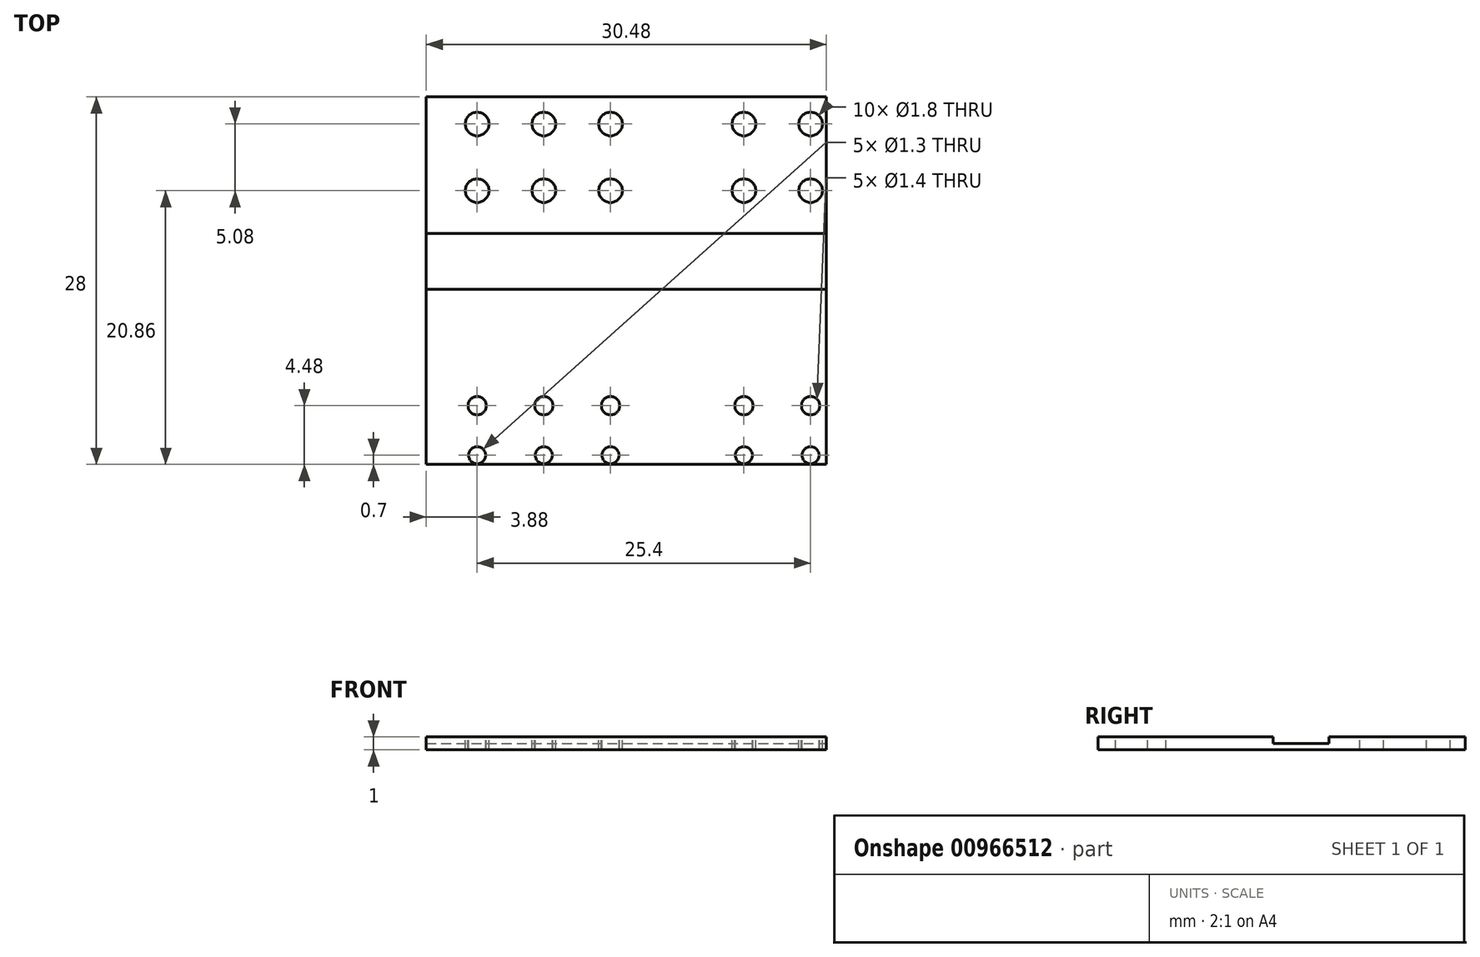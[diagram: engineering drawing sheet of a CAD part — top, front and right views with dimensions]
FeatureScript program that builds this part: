
annotation { "Feature Type Name" : "Feature", "Feature Type Description" : "" }
export const myFeature = defineFeature(function(context is Context, id is Id, definition is map)
    precondition{}
    {
        {
            var Q0;
            Q0=qCreatedBy(makeId("Top.planeOp"),FACE);
            var sketch = newSketch(context, id + "F0", { "sketchPlane" : qUnion([Q0])});
            skLineSegment(sketch, "E0.bottom", {"start": v(-15.24, 14) * mm, "end": v(15.24, 14) * mm});
            skLineSegment(sketch, "E0.top", {"start": v(-15.24, -14) * mm, "end": v(15.24, -14) * mm});
            skLineSegment(sketch, "E0.left", {"start": v(-15.24, 14) * mm, "end": v(-15.24, -14) * mm});
            skLineSegment(sketch, "E0.right", {"start": v(15.24, 14) * mm, "end": v(15.24, -14) * mm});
            skSolve(sketch);
        }
        {
            var Q0;
            Q0 = qSketchRegion(id + "F0", true);
            extrude(context, id + "F1", {"entities" : qUnion([Q0]), "depth" : 1 * mm, "offsetDistance" : 25 * mm});
        }
        {
            var Q0;
            Q0=makeQuery(id+"F1.opExtrude","CAP_FACE",FACE,{"disambiguationData":[OSD([sQuery(id+"F0.wireOp",EDGE,"E0.bottom"),sQuery(id+"F0.wireOp",EDGE,"E0.top"),sQuery(id+"F0.wireOp",EDGE,"E0.left"),sQuery(id+"F0.wireOp",EDGE,"E0.right")])],"isStart":false});
            var sketch = newSketch(context, id + "F2", { "sketchPlane" : qUnion([Q0])});
            skCircle(sketch, "E1", {"center": v(-11.36, 11.94) * mm, "radius": 0.9 * mm});
            skCircle(sketch, "E2", {"center": v(-11.36, 6.86) * mm, "radius": 0.9 * mm});
            skCircle(sketch, "E3", {"center": v(-6.28, 11.94) * mm, "radius": 0.9 * mm});
            skCircle(sketch, "E4", {"center": v(-6.28, 6.86) * mm, "radius": 0.9 * mm});
            skCircle(sketch, "E5", {"center": v(-11.36, -9.52) * mm, "radius": 0.7 * mm});
            skCircle(sketch, "E6", {"center": v(-11.36, -13.3) * mm, "radius": 0.65 * mm});
            skCircle(sketch, "E7", {"center": v(-6.28, -9.52) * mm, "radius": 0.7 * mm});
            skCircle(sketch, "E8", {"center": v(-6.28, -13.3) * mm, "radius": 0.65 * mm});
            skCircle(sketch, "E9", {"center": v(-1.2, 11.94) * mm, "radius": 0.9 * mm});
            skCircle(sketch, "E10", {"center": v(-1.2, 6.86) * mm, "radius": 0.9 * mm});
            skCircle(sketch, "E11", {"center": v(8.96, 11.94) * mm, "radius": 0.9 * mm});
            skCircle(sketch, "E12", {"center": v(8.96, 6.86) * mm, "radius": 0.9 * mm});
            skCircle(sketch, "E13", {"center": v(14.04, 11.94) * mm, "radius": 0.9 * mm});
            skCircle(sketch, "E14", {"center": v(14.04, 6.86) * mm, "radius": 0.9 * mm});
            skCircle(sketch, "E15", {"center": v(-1.2, -9.52) * mm, "radius": 0.7 * mm});
            skCircle(sketch, "E16", {"center": v(-1.2, -13.3) * mm, "radius": 0.65 * mm});
            skCircle(sketch, "E17", {"center": v(8.96, -9.52) * mm, "radius": 0.7 * mm});
            skCircle(sketch, "E18", {"center": v(8.96, -13.3) * mm, "radius": 0.65 * mm});
            skCircle(sketch, "E19", {"center": v(14.04, -9.52) * mm, "radius": 0.7 * mm});
            skCircle(sketch, "E20", {"center": v(14.04, -13.3) * mm, "radius": 0.65 * mm});
            skSolve(sketch);
        }
        {
            var Q0;
            Q0=makeQuery(id+"F1.opExtrude","CAP_FACE",FACE,{"disambiguationData":[OSD([sQuery(id+"F0.wireOp",EDGE,"E0.bottom"),sQuery(id+"F0.wireOp",EDGE,"E0.top"),sQuery(id+"F0.wireOp",EDGE,"E0.left"),sQuery(id+"F0.wireOp",EDGE,"E0.right")])],"isStart":false});
            var sketch = newSketch(context, id + "F3", { "sketchPlane" : qUnion([Q0])});
            skLineSegment(sketch, "E21.bottom", {"start": v(-15.24, 3.61) * mm, "end": v(15.24, 3.61) * mm});
            skLineSegment(sketch, "E21.top", {"start": v(-15.24, -0.65) * mm, "end": v(15.24, -0.65) * mm});
            skLineSegment(sketch, "E21.left", {"start": v(-15.24, 3.61) * mm, "end": v(-15.24, -0.65) * mm});
            skLineSegment(sketch, "E21.right", {"start": v(15.24, 3.61) * mm, "end": v(15.24, -0.65) * mm});
            skSolve(sketch);
        }
        {
            var Q0;
            Q0 = qSketchRegion(id + "F3", true);
            extrude(context, id + "F4", {"entities" : qUnion([Q0]), "operationType" : NewBodyOperationType.REMOVE, "oppositeDirection" : true, "depth" : 0.5 * mm, "offsetDistance" : 25 * mm});
        }
        {
            var Q0;
            Q0=makeQuery(id+"F2.imprint","IMPRINT",FACE,{"disambiguationData":[TD([[makeQuery(id+"F2.imprint","IMPRINT",EDGE,{"derivedFrom":sQuery(id+"F2.wireOp",EDGE,"E1")}),1.0]])]});
            var Q1;
            Q1=makeQuery(id+"F2.imprint","IMPRINT",FACE,{"disambiguationData":[TD([[makeQuery(id+"F2.imprint","IMPRINT",EDGE,{"derivedFrom":sQuery(id+"F2.wireOp",EDGE,"E3")}),1.0]])]});
            var Q2;
            Q2=makeQuery(id+"F2.imprint","IMPRINT",FACE,{"disambiguationData":[TD([[makeQuery(id+"F2.imprint","IMPRINT",EDGE,{"derivedFrom":sQuery(id+"F2.wireOp",EDGE,"E9")}),1.0]])]});
            var Q3;
            Q3=makeQuery(id+"F2.imprint","IMPRINT",FACE,{"disambiguationData":[TD([[makeQuery(id+"F2.imprint","IMPRINT",EDGE,{"derivedFrom":sQuery(id+"F2.wireOp",EDGE,"E11")}),1.0]])]});
            var Q4;
            Q4=makeQuery(id+"F2.imprint","IMPRINT",FACE,{"disambiguationData":[TD([[makeQuery(id+"F2.imprint","IMPRINT",EDGE,{"derivedFrom":sQuery(id+"F2.wireOp",EDGE,"E13")}),1.0]])]});
            var Q5;
            Q5=makeQuery(id+"F2.imprint","IMPRINT",FACE,{"disambiguationData":[TD([[makeQuery(id+"F2.imprint","IMPRINT",EDGE,{"derivedFrom":sQuery(id+"F2.wireOp",EDGE,"E2")}),1.0]])]});
            var Q6;
            Q6=makeQuery(id+"F2.imprint","IMPRINT",FACE,{"disambiguationData":[TD([[makeQuery(id+"F2.imprint","IMPRINT",EDGE,{"derivedFrom":sQuery(id+"F2.wireOp",EDGE,"E4")}),1.0]])]});
            var Q7;
            Q7=makeQuery(id+"F2.imprint","IMPRINT",FACE,{"disambiguationData":[TD([[makeQuery(id+"F2.imprint","IMPRINT",EDGE,{"derivedFrom":sQuery(id+"F2.wireOp",EDGE,"E10")}),1.0]])]});
            var Q8;
            Q8=makeQuery(id+"F2.imprint","IMPRINT",FACE,{"disambiguationData":[TD([[makeQuery(id+"F2.imprint","IMPRINT",EDGE,{"derivedFrom":sQuery(id+"F2.wireOp",EDGE,"E12")}),1.0]])]});
            var Q9;
            Q9=makeQuery(id+"F2.imprint","IMPRINT",FACE,{"disambiguationData":[TD([[makeQuery(id+"F2.imprint","IMPRINT",EDGE,{"derivedFrom":sQuery(id+"F2.wireOp",EDGE,"E14")}),1.0]])]});
            var Q10;
            Q10=makeQuery(id+"F2.imprint","IMPRINT",FACE,{"disambiguationData":[TD([[makeQuery(id+"F2.imprint","IMPRINT",EDGE,{"derivedFrom":sQuery(id+"F2.wireOp",EDGE,"E5")}),1.0]])]});
            var Q11;
            Q11=makeQuery(id+"F2.imprint","IMPRINT",FACE,{"disambiguationData":[TD([[makeQuery(id+"F2.imprint","IMPRINT",EDGE,{"derivedFrom":sQuery(id+"F2.wireOp",EDGE,"E7")}),1.0]])]});
            var Q12;
            Q12=makeQuery(id+"F2.imprint","IMPRINT",FACE,{"disambiguationData":[TD([[makeQuery(id+"F2.imprint","IMPRINT",EDGE,{"derivedFrom":sQuery(id+"F2.wireOp",EDGE,"E15")}),1.0]])]});
            var Q13;
            Q13=makeQuery(id+"F2.imprint","IMPRINT",FACE,{"disambiguationData":[TD([[makeQuery(id+"F2.imprint","IMPRINT",EDGE,{"derivedFrom":sQuery(id+"F2.wireOp",EDGE,"E17")}),1.0]])]});
            var Q14;
            Q14=makeQuery(id+"F2.imprint","IMPRINT",FACE,{"disambiguationData":[TD([[makeQuery(id+"F2.imprint","IMPRINT",EDGE,{"derivedFrom":sQuery(id+"F2.wireOp",EDGE,"E19")}),1.0]])]});
            var Q15;
            Q15=makeQuery(id+"F2.imprint","IMPRINT",FACE,{"disambiguationData":[TD([[makeQuery(id+"F2.imprint","IMPRINT",EDGE,{"derivedFrom":sQuery(id+"F2.wireOp",EDGE,"E6")}),1.0]])]});
            var Q16;
            Q16=makeQuery(id+"F2.imprint","IMPRINT",FACE,{"disambiguationData":[TD([[makeQuery(id+"F2.imprint","IMPRINT",EDGE,{"derivedFrom":sQuery(id+"F2.wireOp",EDGE,"E8")}),1.0]])]});
            var Q17;
            Q17=makeQuery(id+"F2.imprint","IMPRINT",FACE,{"disambiguationData":[TD([[makeQuery(id+"F2.imprint","IMPRINT",EDGE,{"derivedFrom":sQuery(id+"F2.wireOp",EDGE,"E16")}),1.0]])]});
            var Q18;
            Q18=makeQuery(id+"F2.imprint","IMPRINT",FACE,{"disambiguationData":[TD([[makeQuery(id+"F2.imprint","IMPRINT",EDGE,{"derivedFrom":sQuery(id+"F2.wireOp",EDGE,"E18")}),1.0]])]});
            var Q19;
            Q19=makeQuery(id+"F2.imprint","IMPRINT",FACE,{"disambiguationData":[TD([[makeQuery(id+"F2.imprint","IMPRINT",EDGE,{"derivedFrom":sQuery(id+"F2.wireOp",EDGE,"E20")}),1.0]])]});
            extrude(context, id + "F5", {"entities" : qUnion([Q0, Q1, Q2, Q3, Q4, Q5, Q6, Q7, Q8, Q9, Q10, Q11, Q12, Q13, Q14, Q15, Q16, Q17, Q18, Q19]), "operationType" : NewBodyOperationType.REMOVE, "oppositeDirection" : true, "depth" : 2 * mm, "offsetDistance" : 25 * mm});
        }
    });
